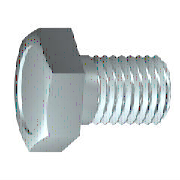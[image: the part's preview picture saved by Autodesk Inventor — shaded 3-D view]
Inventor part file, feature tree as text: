
AUTODESK INVENTOR PART (.ipt)
format: ipt  version: 2021 (Build 250183000, 183)  size: 204,288 bytes
history: native  units: mm (DEFAULTED — no unit token found)
features: sketch x4, extrude x2, chamfer x1, plane x1
ambient origin geometry x7: Origin, YZ Plane, XY Plane, X Axis, Y Axis, Z Axis, Center Point
bodies: Solid1 (feature_tree), Body (feature_tree)
feature tree (8):
  extrude  "Head"  Depth=10.0mm
  extrude  "Indent1"  Depth=17.0mm
  chamfer  "Chamfer1"  Angle=30.0deg  [1 undecoded]
  plane  "Work Plane1"
  sketch  "Sketch1"  dims[d0=10.0mm d1=25.0mm]
  sketch  "Sketch2"  dims[d5=90.0deg d2=17.0mm]
  sketch  "Sketch4"  dims[d4=0.0mm d6=30.0deg d7=30.0deg d13=90.0deg d8=22.0mm d9=0.0mm d11=0.4mm d12=12.75mm d14=1.646mm d15=0.0mm d16=17.0mm d17=17.0mm d18=19.629909mm d20=0.0mm d33=0.0mm d34=0.0mm]
  sketch  "Sketch3"  dims[d3=8.23mm]
note: 1 required parameter value undecoded (feature->parameter linkage not recoverable at this tier; creation-order binding heuristic only, values carry confidence <= 0.55)
